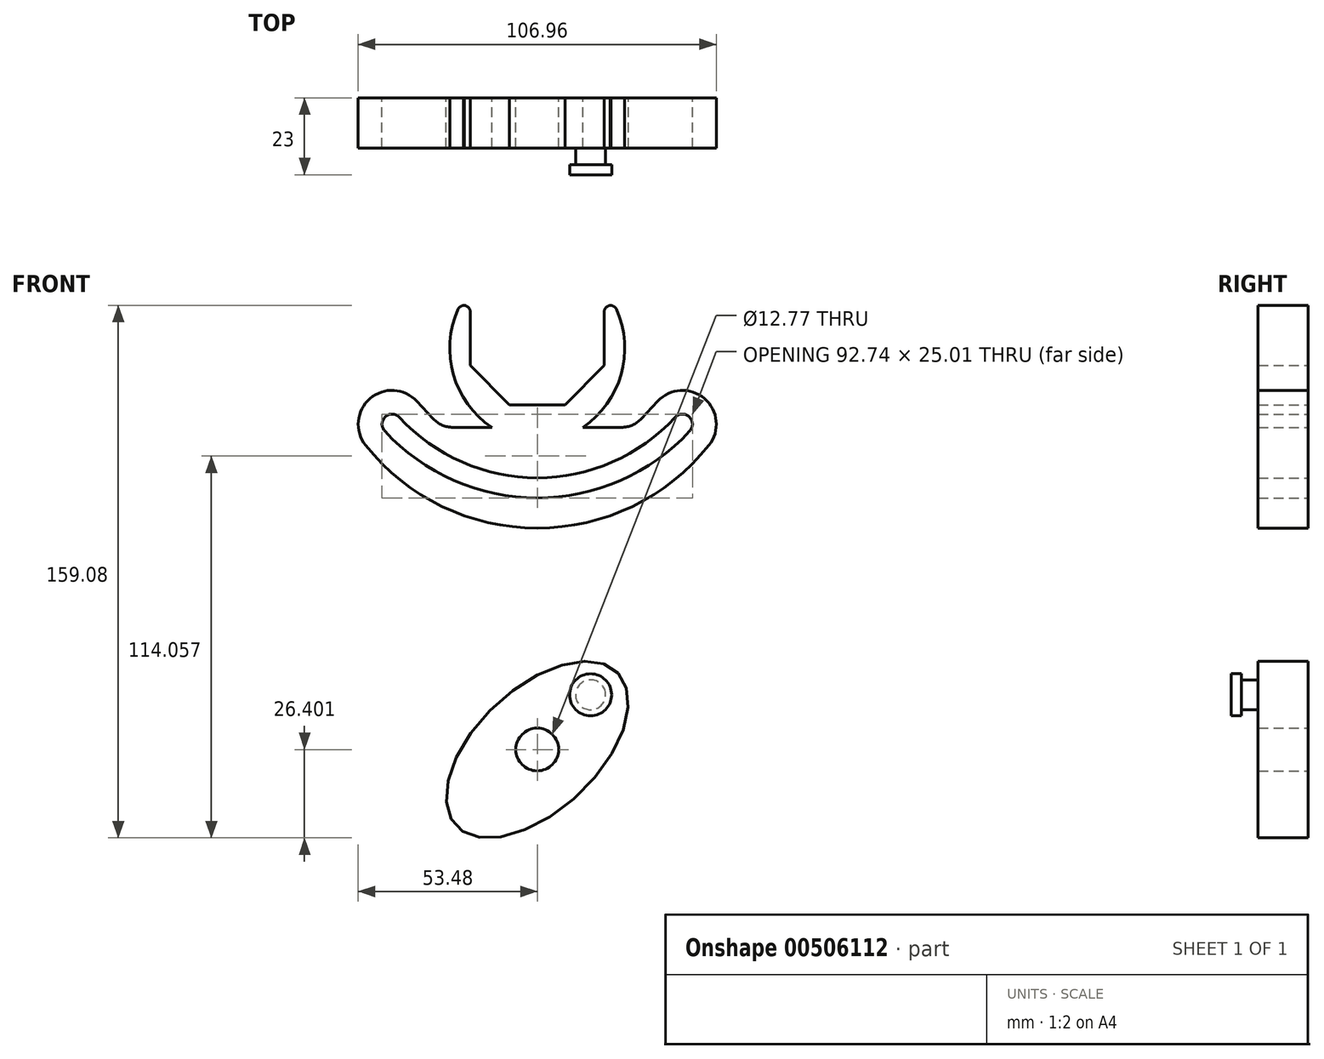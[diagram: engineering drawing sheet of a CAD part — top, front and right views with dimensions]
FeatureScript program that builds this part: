
annotation { "Feature Type Name" : "Feature", "Feature Type Description" : "" }
export const myFeature = defineFeature(function(context is Context, id is Id, definition is map)
    precondition{}
    {
        {
            var Q0;
            Q0=qCreatedBy(makeId("Front.planeOp"),FACE);
            var sketch = newSketch(context, id + "F0", { "sketchPlane" : qUnion([Q0])});
            skCircle(sketch, "E0.cCircle", {"center": v(0, 0) * mm, "radius": 20 * mm, "construction": true});
            skLineSegment(sketch, "E0.0", {"start": v(20, 8.28) * mm, "end": v(20, -8.28) * mm});
            skLineSegment(sketch, "E0.1", {"start": v(20, -8.28) * mm, "end": v(8.28, -20) * mm});
            skLineSegment(sketch, "E0.2", {"start": v(8.28, -20) * mm, "end": v(-8.28, -20) * mm});
            skLineSegment(sketch, "E0.3", {"start": v(-8.28, -20) * mm, "end": v(-20, -8.28) * mm});
            skLineSegment(sketch, "E0.4", {"start": v(-20, -8.28) * mm, "end": v(-20, 7.7) * mm});
            skPoint(sketch, "E0.0.midPoint", {"position": v(20, 0) * mm});
            skPoint(sketch, "E1.orphan", {"position": v(-8.28, 20) * mm});
            skPoint(sketch, "E2.orphan", {"position": v(8.28, 20) * mm});
            skArc(sketch, "E3", {"start": v(-23.63, 8.52) * mm, "mid": v(-25.03, -10.94) * mm, "end": v(-13.59, -26.74) * mm});
            skLineSegment(sketch, "E4", {"start": v(-22, 9.7) * mm, "end": v(-21.8, 9.7) * mm});
            skPoint(sketch, "E5.visualSharp", {"position": v(-20, 9.7) * mm});
            skArc(sketch, "E5.filletArc", {"start": v(-20, 7.7) * mm, "mid": v(-20.59, 9.12) * mm, "end": v(-22, 9.7) * mm});
            skPoint(sketch, "E6.visualSharp", {"position": v(-23.07, 9.7) * mm});
            skArc(sketch, "E6.filletArc", {"start": v(-21.8, 9.7) * mm, "mid": v(-22.9, 9.39) * mm, "end": v(-23.63, 8.52) * mm});
            skLineSegment(sketch, "E7", {"start": v(0, 0) * mm, "end": v(0, 45.63) * mm});
            skArc(sketch, "E8.MirrorCS", {"start": v(23.63, 8.52) * mm, "mid": v(25.03, -10.94) * mm, "end": v(13.59, -26.74) * mm});
            skArc(sketch, "E9.MirrorCS", {"start": v(20, 7.7) * mm, "mid": v(20.59, 9.12) * mm, "end": v(22, 9.7) * mm});
            skLineSegment(sketch, "E10.MirrorCS", {"start": v(22, 9.7) * mm, "end": v(21.8, 9.7) * mm});
            skArc(sketch, "E11.MirrorCS", {"start": v(21.8, 9.7) * mm, "mid": v(22.9, 9.39) * mm, "end": v(23.63, 8.52) * mm});
            skLineSegment(sketch, "E12", {"start": v(-13.59, -26.74) * mm, "end": v(-25.2, -26.74) * mm});
            skLineSegment(sketch, "E13", {"start": v(-31.05, -24.2) * mm, "end": v(-35.97, -18.9) * mm});
            skArc(sketch, "E14", {"start": v(-35.97, -18.9) * mm, "mid": v(-49.97, -18.14) * mm, "end": v(-51.29, -32.1) * mm});
            skLineSegment(sketch, "E15.MirrorCS", {"start": v(13.59, -26.74) * mm, "end": v(25.2, -26.74) * mm});
            skLineSegment(sketch, "E16.MirrorCS", {"start": v(31.05, -24.2) * mm, "end": v(35.97, -18.9) * mm});
            skArc(sketch, "E17.MirrorCS", {"start": v(35.97, -18.9) * mm, "mid": v(49.97, -18.14) * mm, "end": v(51.29, -32.1) * mm});
            skArc(sketch, "E18", {"start": v(-51.29, -32.1) * mm, "mid": v(0, -56.84) * mm, "end": v(51.29, -32.1) * mm});
            skArc(sketch, "E19", {"start": v(-43.37, -25.8) * mm, "mid": v(0, -44.82) * mm, "end": v(43.37, -25.8) * mm, "construction": true});
            skArc(sketch, "E20.0.startCap", {"start": v(-45.58, -27.84) * mm, "mid": v(-45.4, -23.6) * mm, "end": v(-41.16, -23.77) * mm});
            skArc(sketch, "E20.0.endCap", {"start": v(41.16, -23.77) * mm, "mid": v(45.4, -23.6) * mm, "end": v(45.58, -27.84) * mm});
            skArc(sketch, "E20.0.left", {"start": v(-41.16, -23.77) * mm, "mid": v(0, -41.82) * mm, "end": v(41.16, -23.77) * mm});
            skArc(sketch, "E20.0.right", {"start": v(-45.58, -27.84) * mm, "mid": v(0, -47.82) * mm, "end": v(45.58, -27.84) * mm});
            skPoint(sketch, "E21.visualSharp", {"position": v(28.67, -26.74) * mm});
            skArc(sketch, "E21.filletArc", {"start": v(25.2, -26.74) * mm, "mid": v(28.39, -26.08) * mm, "end": v(31.05, -24.2) * mm});
            skPoint(sketch, "E22.visualSharp", {"position": v(-28.67, -26.74) * mm});
            skArc(sketch, "E22.filletArc", {"start": v(-31.05, -24.2) * mm, "mid": v(-28.39, -26.08) * mm, "end": v(-25.2, -26.74) * mm});
            skSolve(sketch);
        }
        {
            var Q0;
            Q0 = qSketchRegion(id + "F0", true);
            extrude(context, id + "F1", {"entities" : qUnion([Q0]), "endBound" : BoundingType.SYMMETRIC, "depth" : 15 * mm});
        }
        {
            var Q0;
            Q0=qCreatedBy(makeId("Front.planeOp"),FACE);
            var sketch = newSketch(context, id + "F2", { "sketchPlane" : qUnion([Q0])});
            skEllipse(sketch, "E23", {"center": v(0, -122.97) * mm, "majorRadius": 33.26 * mm, "minorRadius": 18.23 * mm, "majorAxis": v(0.73, 0.69)});
            skCircle(sketch, "E24", {"center": v(0, -122.97) * mm, "radius": 6.38 * mm});
            skSolve(sketch);
        }
        {
            var Q0;
            Q0 = qSketchRegion(id + "F2", true);
            extrude(context, id + "F3", {"entities" : qUnion([Q0]), "endBound" : BoundingType.SYMMETRIC, "depth" : 15 * mm});
        }
        {
            var Q0;
            Q0=makeQuery(id+"F3.opExtrude","CAP_FACE",FACE,{"disambiguationData":[OSD([sQuery(id+"F2.wireOp",EDGE,"E23"),sQuery(id+"F2.wireOp",EDGE,"E24")])],"isStart":false});
            var sketch = newSketch(context, id + "F4", { "sketchPlane" : qUnion([Q0])});
            skSolve(sketch);
        }
        {
            var Q0;
            Q0=makeQuery(id+"F4.imprint","IMPRINT",FACE,{"disambiguationData":[TD([[makeQuery(id+"F4.imprint","IMPRINT",EDGE,{"derivedFrom":makeQuery(id+"F3.opExtrude","CAP_EDGE",EDGE,{"disambiguationData":[OSD([sQuery(id+"F2.wireOp",EDGE,"E23")])],"isStart":false})}),1.0]])]});
            var sketch = newSketch(context, id + "F5", { "sketchPlane" : qUnion([Q0])});
            skCircle(sketch, "E25", {"center": v(15.93, -106.62) * mm, "radius": 4.48 * mm});
            skSolve(sketch);
        }
        {
            var Q0;
            Q0 = qSketchRegion(id + "F5", true);
            extrude(context, id + "F6", {"entities" : qUnion([Q0]), "operationType" : NewBodyOperationType.ADD, "depth" : 5 * mm});
        }
        {
            var Q0;
            Q0=makeQuery(id+"F6.opExtrude","CAP_FACE",FACE,{"disambiguationData":[OSD([sQuery(id+"F5.wireOp",EDGE,"E25")])],"isStart":false});
            var sketch = newSketch(context, id + "F7", { "sketchPlane" : qUnion([Q0])});
            skCircle(sketch, "E26", {"center": v(15.93, -106.62) * mm, "radius": 6.29 * mm});
            skSolve(sketch);
        }
        {
            var Q0;
            Q0 = qSketchRegion(id + "F7", true);
            extrude(context, id + "F8", {"entities" : qUnion([Q0]), "operationType" : NewBodyOperationType.ADD, "depth" : 3 * mm});
        }
    });
